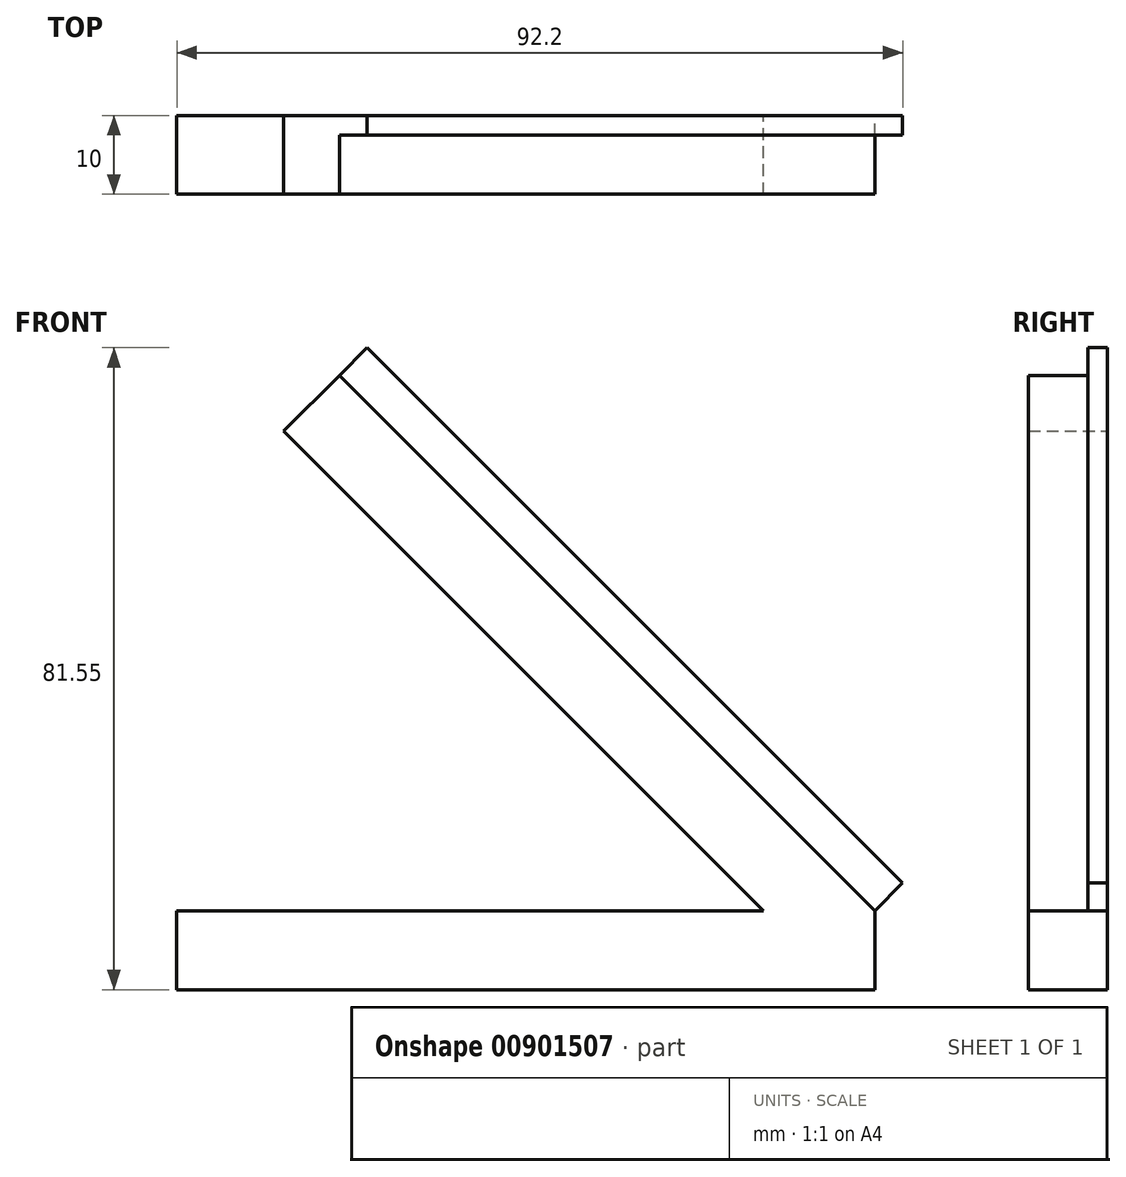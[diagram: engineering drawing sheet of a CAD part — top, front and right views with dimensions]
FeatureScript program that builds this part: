
annotation { "Feature Type Name" : "Feature", "Feature Type Description" : "" }
export const myFeature = defineFeature(function(context is Context, id is Id, definition is map)
    precondition{}
    {
        {
            var Q0;
            Q0=qCreatedBy(makeId("Front.planeOp"),FACE);
            var sketch = newSketch(context, id + "F0", { "sketchPlane" : qUnion([Q0])});
            skLineSegment(sketch, "E0.bottom", {"start": v(0, 0) * mm, "end": v(-88.66, 0) * mm});
            skLineSegment(sketch, "E0.top", {"start": v(0, 10) * mm, "end": v(-88.66, 10) * mm});
            skLineSegment(sketch, "E0.left", {"start": v(0, 0) * mm, "end": v(0, 10) * mm});
            skLineSegment(sketch, "E0.right", {"start": v(-88.66, 0) * mm, "end": v(-88.66, 10) * mm});
            skLineSegment(sketch, "E1", {"start": v(0, 10) * mm, "end": v(-68.01, 78.01) * mm});
            skLineSegment(sketch, "E2", {"start": v(-68.01, 78.01) * mm, "end": v(-75.09, 70.94) * mm});
            skLineSegment(sketch, "E3", {"start": v(-75.09, 70.94) * mm, "end": v(-14.14, 10) * mm});
            skLineSegment(sketch, "E4", {"start": v(-68.01, 78.01) * mm, "end": v(-64.48, 81.55) * mm});
            skLineSegment(sketch, "E5", {"start": v(0, 10) * mm, "end": v(3.54, 13.54) * mm});
            skLineSegment(sketch, "E6", {"start": v(-64.48, 81.55) * mm, "end": v(3.54, 13.54) * mm});
            skSolve(sketch);
        }
        {
            var Q0;
            Q0=makeQuery(id+"F0.imprint","IMPRINT",FACE,{"disambiguationData":[TD([[makeQuery(id+"F0.imprint","IMPRINT",EDGE,{"derivedFrom":sQuery(id+"F0.wireOp",EDGE,"E0.bottom")}),-1.0]])]});
            var Q1;
            {var subQ0=sQuery(id+"F0.wireOp",EDGE,"E1");Q1=makeQuery(id+"F0.imprint","IMPRINT",FACE,{"disambiguationData":[TD([[makeQuery(id+"F0.imprint","IMPRINT",EDGE,{"derivedFrom":subQ0}),1.0]])]});}
            extrude(context, id + "F1", {"entities" : qUnion([Q0, Q1]), "depth" : 10 * mm, "offsetDistance" : 25 * mm});
        }
        {
            var Q0;
            Q0=makeQuery(id+"F0.imprint","IMPRINT",FACE,{"disambiguationData":[TD([[makeQuery(id+"F0.imprint","IMPRINT",EDGE,{"derivedFrom":sQuery(id+"F0.wireOp",EDGE,"E1")}),-1.0]])]});
            extrude(context, id + "F2", {"entities" : qUnion([Q0]), "operationType" : NewBodyOperationType.ADD, "depth" : 2.5 * mm, "offsetDistance" : 25 * mm});
        }
    });
